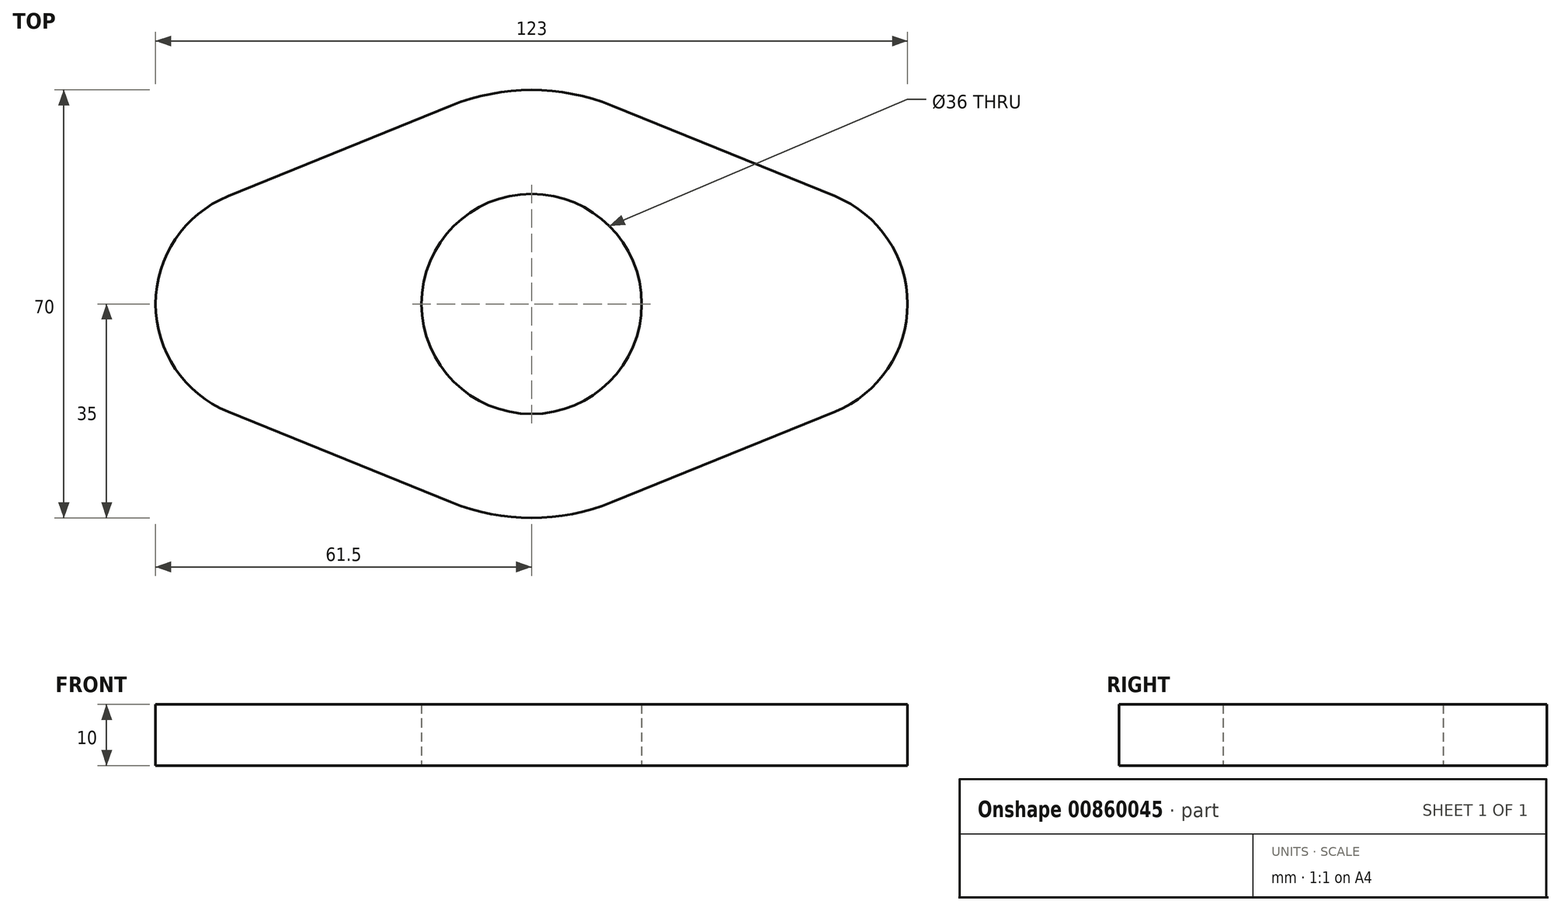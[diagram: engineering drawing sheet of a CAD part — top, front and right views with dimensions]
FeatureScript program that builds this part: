
annotation { "Feature Type Name" : "Feature", "Feature Type Description" : "" }
export const myFeature = defineFeature(function(context is Context, id is Id, definition is map)
    precondition{}
    {
        {
            var Q0;
            Q0=qCreatedBy(makeId("Top.planeOp"),FACE);
            var sketch = newSketch(context, id + "F0", { "sketchPlane" : qUnion([Q0])});
            skArc(sketch, "E0", {"start": v(-13.18, -32.42) * mm, "mid": v(0, -35) * mm, "end": v(13.18, -32.42) * mm});
            skArc(sketch, "E1", {"start": v(-49.65, 17.6) * mm, "mid": v(-61.5, 0) * mm, "end": v(-49.65, -17.6) * mm});
            skCircle(sketch, "E2", {"center": v(0, 0) * mm, "radius": 18 * mm});
            skLineSegment(sketch, "E3", {"start": v(-49.65, 17.6) * mm, "end": v(-13.18, 32.42) * mm});
            skLineSegment(sketch, "E4.MirrorCS", {"start": v(-49.65, -17.6) * mm, "end": v(-13.18, -32.42) * mm});
            skLineSegment(sketch, "E5.MirrorCS", {"start": v(49.65, 17.6) * mm, "end": v(13.18, 32.42) * mm});
            skLineSegment(sketch, "E6.MirrorCS", {"start": v(49.65, -17.6) * mm, "end": v(13.18, -32.42) * mm});
            skArc(sketch, "E7.trimOffspring", {"start": v(13.18, 32.42) * mm, "mid": v(0, 35) * mm, "end": v(-13.18, 32.42) * mm});
            skArc(sketch, "E8.trimOffspring", {"start": v(49.65, 17.6) * mm, "mid": v(61.5, 0) * mm, "end": v(49.65, -17.6) * mm});
            skSolve(sketch);
        }
        {
            var Q0;
            Q0=makeQuery(id+"F0.imprint","IMPRINT",FACE,{"disambiguationData":[TD([[makeQuery(id+"F0.imprint","IMPRINT",EDGE,{"derivedFrom":sQuery(id+"F0.wireOp",EDGE,"E0")}),1.0]])]});
            extrude(context, id + "F1", {"entities" : qUnion([Q0]), "depth" : 10 * mm, "offsetDistance" : 25 * mm});
        }
    });
